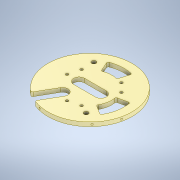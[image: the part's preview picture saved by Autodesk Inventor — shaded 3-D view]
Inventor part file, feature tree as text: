
AUTODESK INVENTOR PART (.ipt)
format: ipt  version: 2021 (Build 250183000, 183)  size: 379,392 bytes
history: native  units: in
note: dims shown in document units (in); Inventor stores cm internally (conversion verified against a paired STEP export)
features: other x14, extrude x5, hole x4, pattern_circular x3, fillet x1
ambient origin geometry x8: Origin, YZ Plane, XZ Plane, XY Plane, X Axis, Y Axis, Z Axis, Center Point
bodies: Solid1 (feature_tree)
feature tree (27):
  other  "End Cap"
  extrude  "Cylinders Cutout"  TaperAngle=0.0deg  [1 undecoded]
  extrude  "Wedges Cutout"  TaperAngle=0.0deg  [1 undecoded]
  extrude  "Rope Holes Cutout"  Depth=7.75in
  extrude  "Support Holes Cutout"  Depth=1.0in
  other  "Set Screw Sketch"
  other  "Edge Hole Plane 1"
  other  "Edge Hole Plane 2"
  other  "Edge Hole Center 1"
  other  "Edge Hole Center 2"
  other  "Central Plane"
  hole  "Insert Edge Hole 1"  [1 undecoded]
  hole  "Insert Edge Hole 2"  [1 undecoded]
  pattern_circular  "Circular Pattern2"  [2 undecoded]
  pattern_circular  "Circular Pattern3"  [2 undecoded]
  extrude  "Cutouts extrude"  Depth=2.0132in
  fillet  "Fillet1"  [1 undecoded]
  other  "Edge Hole Center 1 - Unthreaded"
  other  "Edge Hole Center 2 - Unthreaded"
  hole  "Edge Hole 1 - Unthreaded"  [1 undecoded]
  hole  "Edge Hole 2 - Unthreaded"  [1 undecoded]
  pattern_circular  "Circular Pattern4"  [2 undecoded]
  other  "Cylinders Sketch"
  other  "Wedges Sketch"
  other  "Rope Holes Sketch"
  other  "Support Holes Sketch"
  other  "Cutouts"
note: 13 required parameter values undecoded (feature->parameter linkage not recoverable at this tier; creation-order binding heuristic only, values carry confidence <= 0.55)
